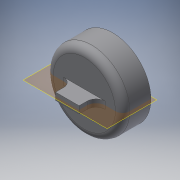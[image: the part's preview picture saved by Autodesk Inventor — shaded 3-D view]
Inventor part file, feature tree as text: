
AUTODESK INVENTOR PART (.ipt)
format: ipt  version: 2017 (Build 210142000, 142)  size: 145,920 bytes
history: native  units: in
note: dims shown in document units (in); Inventor stores cm internally (conversion verified against a paired STEP export)
features: other x4, sketch x3, extrude x3, plane x2, fillet x2, reference x1, projected_geometry x1
ambient origin geometry x8: Origin, YZ Plane, XZ Plane, XY Plane, X Axis, Y Axis, Z Axis, Center Point
bodies: Body1 (feature_tree)
feature tree (16):
  sketch  "Sketch1"  dims[d4=0.1575in d5=0.0in d6=0.1181in d7=0.0in]
  plane  "Work Plane1"
  extrude  "Extrusion2"  Depth=0.1181in TaperAngle=0.0deg
  extrude  "Extrusion3"  Depth=0.315in TaperAngle=0.0deg
  extrude  "Extrusion4"  Depth=0.1in
  fillet  "Fillet1"  Radius=0.1in
  fillet  "Fillet2"  [1 undecoded]
  plane  "Work Plane2"
  reference  "Reference1"
  sketch  "Sketch2"  dims[d10=0.1in d11=0.315in d12=0.0in]
  projected_geometry  "Projected Loop1"
  sketch  "Sketch3"  dims[d13=0.125in d14=0.0984in d15=0.1in d16=90.0deg]
  other  "Work Axis1"
  other  "Rubiks Arm Assembly.iam"
  other  "8mmx22mm bearing:3"
  other  "Solenoid:1"
note: 1 required parameter value undecoded (feature->parameter linkage not recoverable at this tier; creation-order binding heuristic only, values carry confidence <= 0.55)
